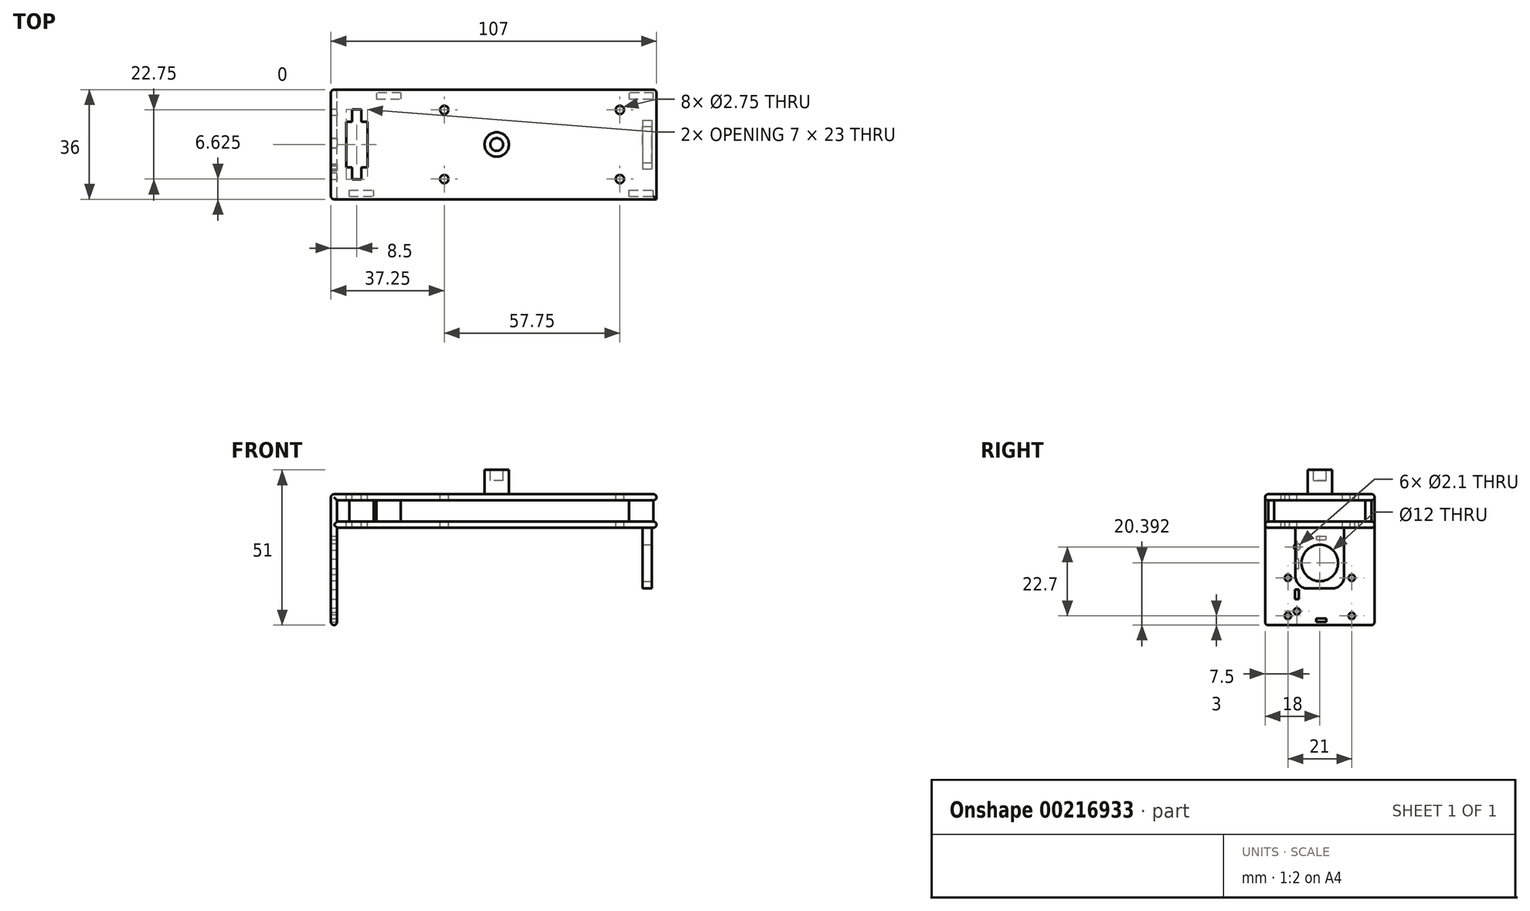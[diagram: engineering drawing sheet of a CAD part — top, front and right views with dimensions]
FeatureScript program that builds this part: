
annotation { "Feature Type Name" : "Feature", "Feature Type Description" : "" }
export const myFeature = defineFeature(function(context is Context, id is Id, definition is map)
    precondition{}
    {
        {
            var Q0;
            Q0=qCreatedBy(makeId("Front.planeOp"),FACE);
            var sketch = newSketch(context, id + "F0", { "sketchPlane" : qUnion([Q0])});
            skLineSegment(sketch, "E0.bottom", {"start": v(0, 0) * mm, "end": v(-2, 0) * mm});
            skLineSegment(sketch, "E0.top", {"start": v(0, -43) * mm, "end": v(-2, -43) * mm});
            skLineSegment(sketch, "E0.left", {"start": v(0, 0) * mm, "end": v(0, -43) * mm});
            skLineSegment(sketch, "E0.right", {"start": v(-2, 0) * mm, "end": v(-2, -43) * mm});
            skLineSegment(sketch, "E1.bottom", {"start": v(0, 0) * mm, "end": v(105, 0) * mm});
            skLineSegment(sketch, "E1.top", {"start": v(0, -2) * mm, "end": v(105, -2) * mm});
            skLineSegment(sketch, "E1.left", {"start": v(0, 0) * mm, "end": v(0, -2) * mm});
            skLineSegment(sketch, "E1.right", {"start": v(105, 0) * mm, "end": v(105, -2) * mm});
            skPoint(sketch, "E2.oppositeSnap0", {"position": v(0, -11) * mm});
            skLineSegment(sketch, "E2.bottom", {"start": v(0, -9) * mm, "end": v(105, -9) * mm});
            skLineSegment(sketch, "E2.top", {"start": v(0, -11) * mm, "end": v(105, -11) * mm});
            skLineSegment(sketch, "E2.left", {"start": v(0, -9) * mm, "end": v(0, -11) * mm});
            skLineSegment(sketch, "E2.right", {"start": v(105, -9) * mm, "end": v(105, -11) * mm});
            skSolve(sketch);
        }
        {
            var Q0;
            Q0 = qSketchRegion(id + "F0", true);
            extrude(context, id + "F1", {"entities" : qUnion([Q0]), "endBound" : BoundingType.SYMMETRIC, "depth" : 36 * mm});
        }
        {
            var Q0;
            Q0=makeQuery(id+"F1.opExtrude","SWEPT_FACE",FACE,{"disambiguationData":[OSD([sQuery(id+"F0.wireOp",EDGE,"E0.bottom"),sQuery(id+"F0.wireOp",EDGE,"E1.bottom")])]});
            var sketch = newSketch(context, id + "F2", { "sketchPlane" : qUnion([Q0])});
            skCircle(sketch, "E3", {"center": v(52.5, 0) * mm, "radius": 4 * mm});
            skSolve(sketch);
        }
        {
            var Q0;
            Q0 = qSketchRegion(id + "F2", true);
            extrude(context, id + "F3", {"entities" : qUnion([Q0]), "operationType" : NewBodyOperationType.ADD, "depth" : 8 * mm});
        }
        {
            var Q0;
            Q0=makeQuery(id+"F3.opExtrude","CAP_FACE",FACE,{"disambiguationData":[OSD([sQuery(id+"F2.wireOp",EDGE,"E3")])],"isStart":false});
            var sketch = newSketch(context, id + "F4", { "sketchPlane" : qUnion([Q0])});
            skCircle(sketch, "E4", {"center": v(52.5, 0) * mm, "radius": 2.1 * mm});
            skSolve(sketch);
        }
        {
            var Q0;
            Q0 = qSketchRegion(id + "F4", true);
            extrude(context, id + "F5", {"entities" : qUnion([Q0]), "operationType" : NewBodyOperationType.REMOVE, "oppositeDirection" : true, "depth" : 3.5 * mm});
        }
        {
            var Q0;
            Q0=makeQuery(id+"F1.opExtrude","SWEPT_FACE",FACE,{"disambiguationData":[OSD([sQuery(id+"F0.wireOp",EDGE,"E0.right")])]});
            var sketch = newSketch(context, id + "F6", { "sketchPlane" : qUnion([Q0])});
            skCircle(sketch, "E5", {"center": v(-10.5, -40) * mm, "radius": 1.05 * mm});
            skCircle(sketch, "E6", {"center": v(10.5, -40) * mm, "radius": 1.05 * mm});
            skCircle(sketch, "E7", {"center": v(-10.5, -27.5) * mm, "radius": 1.05 * mm});
            skCircle(sketch, "E8", {"center": v(10.5, -27.5) * mm, "radius": 1.05 * mm});
            skSolve(sketch);
        }
        {
            var Q0;
            Q0 = qSketchRegion(id + "F6", true);
            var Q1;
            {var subQ0=sQuery(id+"F0.wireOp",EDGE,"E0.left");Q1=makeQuery(id+"F1.opExtrude","SWEPT_FACE",FACE,{"disambiguationData":[OSD([subQ0]),TDD([makeQuery(id+"F0.imprint","IMPRINT",EDGE,{"disambiguationData":[TD([[makeQuery(id+"F0.imprint","INTERSECT",VERTEX,{"derivedFrom":[sQuery(id+"F0.wireOp",EDGE,"E0.top"),subQ0]}),1.0]])],"derivedFrom":subQ0})])]});}
            extrude(context, id + "F7", {"entities" : qUnion([Q0]), "operationType" : NewBodyOperationType.REMOVE, "endBound" : BoundingType.UP_TO_SURFACE, "oppositeDirection" : true, "endBoundEntityFace" : qUnion([Q1]), "depth" : 25 * mm});
        }
        {
            var Q0;
            Q0=makeQuery(id+"F1.opExtrude","SWEPT_FACE",FACE,{"disambiguationData":[OSD([sQuery(id+"F0.wireOp",EDGE,"E0.bottom"),sQuery(id+"F0.wireOp",EDGE,"E1.bottom")])]});
            var sketch = newSketch(context, id + "F8", { "sketchPlane" : qUnion([Q0])});
            skCircle(sketch, "E9", {"center": v(35.25, 11.37) * mm, "radius": 1.38 * mm});
            skCircle(sketch, "E10", {"center": v(35.25, -11.37) * mm, "radius": 1.38 * mm});
            skCircle(sketch, "E11", {"center": v(93, 11.38) * mm, "radius": 1.38 * mm});
            skCircle(sketch, "E12", {"center": v(93, -11.38) * mm, "radius": 1.38 * mm});
            skSolve(sketch);
        }
        {
            var Q0;
            Q0 = qSketchRegion(id + "F8", true);
            var Q1;
            Q1=makeQuery(id+"F1.opExtrude","SWEPT_FACE",FACE,{"disambiguationData":[OSD([sQuery(id+"F0.wireOp",EDGE,"E2.top")])]});
            extrude(context, id + "F9", {"entities" : qUnion([Q0]), "operationType" : NewBodyOperationType.REMOVE, "endBound" : BoundingType.UP_TO_SURFACE, "oppositeDirection" : true, "endBoundEntityFace" : qUnion([Q1]), "depth" : 25 * mm});
        }
        {
            var Q0;
            Q0=makeQuery(id+"F1.opExtrude","SWEPT_FACE",FACE,{"disambiguationData":[OSD([sQuery(id+"F0.wireOp",EDGE,"E0.bottom"),sQuery(id+"F0.wireOp",EDGE,"E1.bottom")])]});
            var sketch = newSketch(context, id + "F10", { "sketchPlane" : qUnion([Q0])});
            skLineSegment(sketch, "E13.bottom", {"start": v(3, 7.5) * mm, "end": v(10, 7.5) * mm});
            skLineSegment(sketch, "E13.top", {"start": v(3, -7.5) * mm, "end": v(10, -7.5) * mm});
            skLineSegment(sketch, "E13.left", {"start": v(3, 7.5) * mm, "end": v(3, -7.5) * mm});
            skLineSegment(sketch, "E13.right", {"start": v(10, 7.5) * mm, "end": v(10, -7.5) * mm});
            skLineSegment(sketch, "E14.bottom", {"start": v(6.5, 7.5) * mm, "end": v(8, 7.5) * mm});
            skLineSegment(sketch, "E14.top", {"start": v(5, 11.5) * mm, "end": v(8, 11.5) * mm});
            skLineSegment(sketch, "E14.left", {"start": v(5, 7.5) * mm, "end": v(5, 11.5) * mm});
            skLineSegment(sketch, "E14.right", {"start": v(8, 7.5) * mm, "end": v(8, 11.5) * mm});
            skLineSegment(sketch, "E15.bottom", {"start": v(5, -7.5) * mm, "end": v(8, -7.5) * mm});
            skLineSegment(sketch, "E15.top", {"start": v(5, -11.5) * mm, "end": v(8, -11.5) * mm});
            skLineSegment(sketch, "E15.left", {"start": v(5, -7.5) * mm, "end": v(5, -11.5) * mm});
            skLineSegment(sketch, "E15.right", {"start": v(8, -7.5) * mm, "end": v(8, -11.5) * mm});
            skLineSegment(sketch, "E16", {"start": v(5, 7.5) * mm, "end": v(8, 7.5) * mm});
            skSolve(sketch);
        }
        {
            var Q0;
            Q0 = qSketchRegion(id + "F10", true);
            var Q1;
            Q1=makeQuery(id+"F1.opExtrude","SWEPT_FACE",FACE,{"disambiguationData":[OSD([sQuery(id+"F0.wireOp",EDGE,"E2.top")])]});
            extrude(context, id + "F11", {"entities" : qUnion([Q0]), "operationType" : NewBodyOperationType.REMOVE, "endBound" : BoundingType.UP_TO_SURFACE, "oppositeDirection" : true, "endBoundEntityFace" : qUnion([Q1]), "depth" : 25 * mm});
        }
        {
            var Q0;
            Q0=makeQuery(id+"F1.opExtrude","SWEPT_EDGE",EDGE,{"disambiguationData":[OSD([sQuery(id+"F0.wireOp",EDGE,"E0.bottom"),sQuery(id+"F0.wireOp",EDGE,"E0.right")])]});
            var Q1;
            Q1=makeQuery(id+"F1.opExtrude","CAP_EDGE",EDGE,{"disambiguationData":[OSD([sQuery(id+"F0.wireOp",EDGE,"E0.bottom"),sQuery(id+"F0.wireOp",EDGE,"E1.bottom")])],"isStart":false});
            var Q2;
            Q2=makeQuery(id+"F1.opExtrude","CAP_EDGE",EDGE,{"disambiguationData":[OSD([sQuery(id+"F0.wireOp",EDGE,"E0.bottom"),sQuery(id+"F0.wireOp",EDGE,"E1.bottom")])],"isStart":true});
            var Q3;
            Q3=makeQuery(id+"F1.opExtrude","SWEPT_EDGE",EDGE,{"disambiguationData":[OSD([sQuery(id+"F0.wireOp",EDGE,"E1.bottom"),sQuery(id+"F0.wireOp",EDGE,"E1.right")])]});
            var Q4;
            Q4=makeQuery(id+"F1.opExtrude","SWEPT_EDGE",EDGE,{"disambiguationData":[OSD([sQuery(id+"F0.wireOp",EDGE,"E1.top"),sQuery(id+"F0.wireOp",EDGE,"E1.right")])]});
            var Q5;
            Q5=makeQuery(id+"F1.opExtrude","SWEPT_EDGE",EDGE,{"disambiguationData":[OSD([sQuery(id+"F0.wireOp",EDGE,"E2.bottom"),sQuery(id+"F0.wireOp",EDGE,"E2.right")])]});
            var Q6;
            Q6=makeQuery(id+"F1.opExtrude","SWEPT_EDGE",EDGE,{"disambiguationData":[OSD([sQuery(id+"F0.wireOp",EDGE,"E2.top"),sQuery(id+"F0.wireOp",EDGE,"E2.right")])]});
            var Q7;
            Q7=makeQuery(id+"F1.opExtrude","CAP_EDGE",EDGE,{"disambiguationData":[OSD([sQuery(id+"F0.wireOp",EDGE,"E2.bottom")])],"isStart":false});
            var Q8;
            Q8=makeQuery(id+"F1.opExtrude","CAP_EDGE",EDGE,{"disambiguationData":[OSD([sQuery(id+"F0.wireOp",EDGE,"E2.top")])],"isStart":false});
            var Q9;
            Q9=makeQuery(id+"F1.opExtrude","CAP_EDGE",EDGE,{"disambiguationData":[OSD([sQuery(id+"F0.wireOp",EDGE,"E1.top")])],"isStart":false});
            var Q10;
            {var subQ0=sQuery(id+"F0.wireOp",EDGE,"E0.left");Q10=makeQuery(id+"F1.opExtrude","CAP_EDGE",EDGE,{"disambiguationData":[OSD([subQ0]),TDD([makeQuery(id+"F0.imprint","IMPRINT",EDGE,{"disambiguationData":[TD([[makeQuery(id+"F0.imprint","INTERSECT",VERTEX,{"derivedFrom":[sQuery(id+"F0.wireOp",EDGE,"E0.top"),subQ0]}),1.0]])],"derivedFrom":subQ0})])],"isStart":false});}
            var Q11;
            Q11=makeQuery(id+"F1.opExtrude","CAP_EDGE",EDGE,{"disambiguationData":[OSD([sQuery(id+"F0.wireOp",EDGE,"E0.right")])],"isStart":false});
            var Q12;
            Q12=makeQuery(id+"F1.opExtrude","SWEPT_EDGE",EDGE,{"disambiguationData":[OSD([sQuery(id+"F0.wireOp",EDGE,"E0.top"),sQuery(id+"F0.wireOp",EDGE,"E0.left")])]});
            var Q13;
            Q13=makeQuery(id+"F1.opExtrude","CAP_EDGE",EDGE,{"disambiguationData":[OSD([sQuery(id+"F0.wireOp",EDGE,"E0.top")])],"isStart":false});
            var Q14;
            Q14=makeQuery(id+"F1.opExtrude","CAP_EDGE",EDGE,{"disambiguationData":[OSD([sQuery(id+"F0.wireOp",EDGE,"E1.top")])],"isStart":true});
            var Q15;
            Q15=makeQuery(id+"F1.opExtrude","CAP_EDGE",EDGE,{"disambiguationData":[OSD([sQuery(id+"F0.wireOp",EDGE,"E2.bottom")])],"isStart":true});
            var Q16;
            Q16=makeQuery(id+"F1.opExtrude","CAP_EDGE",EDGE,{"disambiguationData":[OSD([sQuery(id+"F0.wireOp",EDGE,"E2.top")])],"isStart":true});
            var Q17;
            Q17=makeQuery(id+"F1.opExtrude","CAP_EDGE",EDGE,{"disambiguationData":[OSD([sQuery(id+"F0.wireOp",EDGE,"E1.right")])],"isStart":true});
            var Q18;
            Q18=makeQuery(id+"F1.opExtrude","CAP_EDGE",EDGE,{"disambiguationData":[OSD([sQuery(id+"F0.wireOp",EDGE,"E2.right")])],"isStart":true});
            var Q19;
            {var subQ0=sQuery(id+"F0.wireOp",EDGE,"E0.left");Q19=makeQuery(id+"F1.opExtrude","CAP_EDGE",EDGE,{"disambiguationData":[OSD([subQ0]),TDD([makeQuery(id+"F0.imprint","IMPRINT",EDGE,{"disambiguationData":[TD([[makeQuery(id+"F0.imprint","INTERSECT",VERTEX,{"derivedFrom":[sQuery(id+"F0.wireOp",EDGE,"E0.top"),subQ0]}),1.0]])],"derivedFrom":subQ0})])],"isStart":true});}
            var Q20;
            {var subQ0=sQuery(id+"F0.wireOp",EDGE,"E0.left");Q20=makeQuery(id+"F1.opExtrude","CAP_EDGE",EDGE,{"disambiguationData":[OSD([subQ0]),TDD([makeQuery(id+"F0.imprint","IMPRINT",EDGE,{"disambiguationData":[TD([[makeQuery(id+"F0.imprint","INTERSECT",VERTEX,{"derivedFrom":[subQ0,sQuery(id+"F0.wireOp",EDGE,"E1.top"),sQuery(id+"F0.wireOp",EDGE,"E1.left")]}),-1.0]])],"derivedFrom":subQ0})])],"isStart":true});}
            var Q21;
            Q21=makeQuery(id+"F1.opExtrude","CAP_EDGE",EDGE,{"disambiguationData":[OSD([sQuery(id+"F0.wireOp",EDGE,"E0.right")])],"isStart":true});
            var Q22;
            Q22=makeQuery(id+"F1.opExtrude","CAP_EDGE",EDGE,{"disambiguationData":[OSD([sQuery(id+"F0.wireOp",EDGE,"E0.top")])],"isStart":true});
            var Q23;
            Q23=makeQuery(id+"F1.opExtrude","SWEPT_EDGE",EDGE,{"disambiguationData":[OSD([sQuery(id+"F0.wireOp",EDGE,"E0.top"),sQuery(id+"F0.wireOp",EDGE,"E0.right")])]});
            var Q24;
            {var subQ0=sQuery(id+"F0.wireOp",EDGE,"E0.left");Q24=makeQuery(id+"F1.opExtrude","CAP_EDGE",EDGE,{"disambiguationData":[OSD([subQ0]),TDD([makeQuery(id+"F0.imprint","IMPRINT",EDGE,{"disambiguationData":[TD([[makeQuery(id+"F0.imprint","INTERSECT",VERTEX,{"derivedFrom":[subQ0,sQuery(id+"F0.wireOp",EDGE,"E1.top"),sQuery(id+"F0.wireOp",EDGE,"E1.left")]}),-1.0]])],"derivedFrom":subQ0})])],"isStart":false});}
            fillet(context, id + "F12", {"entities" : qUnion([Q0, Q1, Q2, Q3, Q4, Q5, Q6, Q7, Q8, Q9, Q10, Q11, Q12, Q13, Q14, Q15, Q16, Q17, Q18, Q19, Q20, Q21, Q22, Q23, Q24]), "radius" : 1 * mm, "tangentPropagation" : true, "allowEdgeOverflow" : false});
        }
        {
            var Q0;
            Q0=makeQuery(id+"F1.opExtrude","SWEPT_FACE",FACE,{"disambiguationData":[OSD([sQuery(id+"F0.wireOp",EDGE,"E2.top")])]});
            var sketch = newSketch(context, id + "F13", { "sketchPlane" : qUnion([Q0])});
            skLineSegment(sketch, "E17.bottom", {"start": v(100.5, -8) * mm, "end": v(103.5, -8) * mm});
            skLineSegment(sketch, "E17.top", {"start": v(100.5, 8) * mm, "end": v(103.5, 8) * mm});
            skLineSegment(sketch, "E17.left", {"start": v(100.5, -8) * mm, "end": v(100.5, 8) * mm});
            skLineSegment(sketch, "E17.right", {"start": v(103.5, -8) * mm, "end": v(103.5, 8) * mm});
            skPoint(sketch, "E17.middle", {"position": v(102, 0) * mm});
            skSolve(sketch);
        }
        {
            var Q0;
            Q0 = qSketchRegion(id + "F13", true);
            extrude(context, id + "F14", {"entities" : qUnion([Q0]), "operationType" : NewBodyOperationType.ADD, "depth" : 20 * mm});
        }
        {
            var Q0;
            Q0=makeQuery(id+"F14.opExtrude","CAP_EDGE",EDGE,{"disambiguationData":[OSD([sQuery(id+"F13.wireOp",EDGE,"E17.top")])],"isStart":false});
            var Q1;
            Q1=makeQuery(id+"F14.opExtrude","CAP_EDGE",EDGE,{"disambiguationData":[OSD([sQuery(id+"F13.wireOp",EDGE,"E17.bottom")])],"isStart":false});
            fillet(context, id + "F15", {"entities" : qUnion([Q0, Q1]), "radius" : 4 * mm, "tangentPropagation" : true, "allowEdgeOverflow" : false});
        }
        {
            var Q0;
            Q0=makeQuery(id+"F14.opExtrude","SWEPT_FACE",FACE,{"disambiguationData":[OSD([sQuery(id+"F13.wireOp",EDGE,"E17.right")])]});
            var sketch = newSketch(context, id + "F16", { "sketchPlane" : qUnion([Q0])});
            skCircle(sketch, "E18", {"center": v(0, -22.6) * mm, "radius": 6 * mm});
            skSolve(sketch);
        }
        {
            var Q0;
            Q0 = qSketchRegion(id + "F16", true);
            var Q1;
            Q1=makeQuery(id+"F14.opExtrude","SWEPT_FACE",FACE,{"disambiguationData":[OSD([sQuery(id+"F13.wireOp",EDGE,"E17.left")])]});
            extrude(context, id + "F17", {"entities" : qUnion([Q0]), "operationType" : NewBodyOperationType.REMOVE, "endBound" : BoundingType.UP_TO_SURFACE, "oppositeDirection" : true, "endBoundEntityFace" : qUnion([Q1]), "depth" : 25 * mm});
        }
        {
            var Q0;
            {var subQ0=sQuery(id+"F0.wireOp",EDGE,"E0.left");Q0=makeQuery(id+"F1.opExtrude","SWEPT_FACE",FACE,{"disambiguationData":[OSD([subQ0]),TDD([makeQuery(id+"F0.imprint","IMPRINT",EDGE,{"disambiguationData":[TD([[makeQuery(id+"F0.imprint","INTERSECT",VERTEX,{"derivedFrom":[sQuery(id+"F0.wireOp",EDGE,"E0.top"),subQ0]}),1.0]])],"derivedFrom":subQ0})])]});}
            var sketch = newSketch(context, id + "F18", { "sketchPlane" : qUnion([Q0])});
            skLineSegment(sketch, "E19.bottom", {"start": v(-6.85, -21.3) * mm, "end": v(-6.85, -24.5) * mm});
            skLineSegment(sketch, "E19.top", {"start": v(-8.05, -21.3) * mm, "end": v(-8.05, -24.5) * mm});
            skLineSegment(sketch, "E19.left", {"start": v(-6.85, -21.3) * mm, "end": v(-8.05, -21.3) * mm});
            skLineSegment(sketch, "E19.right", {"start": v(-6.85, -24.5) * mm, "end": v(-8.05, -24.5) * mm});
            skLineSegment(sketch, "E20.bottom", {"start": v(-6.95, -31.3) * mm, "end": v(-6.95, -34.5) * mm});
            skLineSegment(sketch, "E20.top", {"start": v(-8.15, -31.3) * mm, "end": v(-8.15, -34.5) * mm});
            skLineSegment(sketch, "E20.left", {"start": v(-6.95, -31.3) * mm, "end": v(-8.15, -31.3) * mm});
            skLineSegment(sketch, "E20.right", {"start": v(-6.95, -34.5) * mm, "end": v(-8.15, -34.5) * mm});
            skLineSegment(sketch, "E21.bottom", {"start": v(2.05, -40.8) * mm, "end": v(2.05, -42) * mm});
            skLineSegment(sketch, "E21.top", {"start": v(-1.15, -40.8) * mm, "end": v(-1.15, -42) * mm});
            skLineSegment(sketch, "E21.left", {"start": v(2.05, -40.8) * mm, "end": v(-1.15, -40.8) * mm});
            skLineSegment(sketch, "E21.right", {"start": v(2.05, -42) * mm, "end": v(-1.15, -42) * mm});
            skLineSegment(sketch, "E22.bottom", {"start": v(2.15, -13.8) * mm, "end": v(2.15, -15) * mm});
            skLineSegment(sketch, "E22.top", {"start": v(-1.05, -13.8) * mm, "end": v(-1.05, -15) * mm});
            skLineSegment(sketch, "E22.left", {"start": v(2.15, -13.8) * mm, "end": v(-1.05, -13.8) * mm});
            skLineSegment(sketch, "E22.right", {"start": v(2.15, -15) * mm, "end": v(-1.05, -15) * mm});
            skLineSegment(sketch, "E23", {"start": v(0, -11) * mm, "end": v(0, -42) * mm, "construction": true});
            skCircle(sketch, "E24", {"center": v(-7.45, -17.3) * mm, "radius": 1.05 * mm});
            skCircle(sketch, "E25", {"center": v(-7.55, -38.5) * mm, "radius": 1.05 * mm});
            skSolve(sketch);
        }
        {
            var Q0;
            Q0 = qSketchRegion(id + "F18", true);
            var Q1;
            Q1=makeQuery(id+"F1.opExtrude","SWEPT_FACE",FACE,{"disambiguationData":[OSD([sQuery(id+"F0.wireOp",EDGE,"E0.right")])]});
            extrude(context, id + "F19", {"entities" : qUnion([Q0]), "operationType" : NewBodyOperationType.REMOVE, "endBound" : BoundingType.UP_TO_SURFACE, "oppositeDirection" : true, "endBoundEntityFace" : qUnion([Q1]), "depth" : 1.1 * mm});
        }
        {
            var Q0;
            Q0=makeQuery(id+"F1.opExtrude","SWEPT_FACE",FACE,{"disambiguationData":[OSD([sQuery(id+"F0.wireOp",EDGE,"E0.bottom"),sQuery(id+"F0.wireOp",EDGE,"E1.bottom")])]});
            var sketch = newSketch(context, id + "F20", { "sketchPlane" : qUnion([Q0])});
            skLineSegment(sketch, "E26.bottom", {"start": v(13, 17) * mm, "end": v(21, 17) * mm});
            skLineSegment(sketch, "E26.top", {"start": v(13, 15) * mm, "end": v(21, 15) * mm});
            skLineSegment(sketch, "E26.left", {"start": v(13, 17) * mm, "end": v(13, 15) * mm});
            skLineSegment(sketch, "E26.right", {"start": v(21, 17) * mm, "end": v(21, 15) * mm});
            skLineSegment(sketch, "E27.bottom", {"start": v(96, 17) * mm, "end": v(104, 17) * mm});
            skLineSegment(sketch, "E27.top", {"start": v(96, 15) * mm, "end": v(104, 15) * mm});
            skLineSegment(sketch, "E27.left", {"start": v(96, 17) * mm, "end": v(96, 15) * mm});
            skLineSegment(sketch, "E27.right", {"start": v(104, 17) * mm, "end": v(104, 15) * mm});
            skLineSegment(sketch, "E28.MirrorCS", {"start": v(104, -17) * mm, "end": v(104, -15) * mm});
            skLineSegment(sketch, "E29.MirrorCS", {"start": v(96, -17) * mm, "end": v(104, -17) * mm});
            skLineSegment(sketch, "E30.MirrorCS", {"start": v(96, -15) * mm, "end": v(104, -15) * mm});
            skLineSegment(sketch, "E31.MirrorCS", {"start": v(96, -17) * mm, "end": v(96, -15) * mm});
            skLineSegment(sketch, "E32.bottom", {"start": v(4, -17) * mm, "end": v(12, -17) * mm});
            skLineSegment(sketch, "E32.top", {"start": v(4, -15) * mm, "end": v(12, -15) * mm});
            skLineSegment(sketch, "E32.left", {"start": v(4, -17) * mm, "end": v(4, -15) * mm});
            skLineSegment(sketch, "E32.right", {"start": v(12, -17) * mm, "end": v(12, -15) * mm});
            skSolve(sketch);
        }
        {
            var Q0;
            Q0 = qSketchRegion(id + "F20", true);
            var Q1;
            Q1=makeQuery(id+"F1.opExtrude","SWEPT_FACE",FACE,{"disambiguationData":[OSD([sQuery(id+"F0.wireOp",EDGE,"E2.top")])]});
            extrude(context, id + "F21", {"entities" : qUnion([Q0]), "operationType" : NewBodyOperationType.ADD, "endBound" : BoundingType.UP_TO_SURFACE, "oppositeDirection" : true, "endBoundEntityFace" : qUnion([Q1]), "depth" : 25 * mm});
        }
    });
